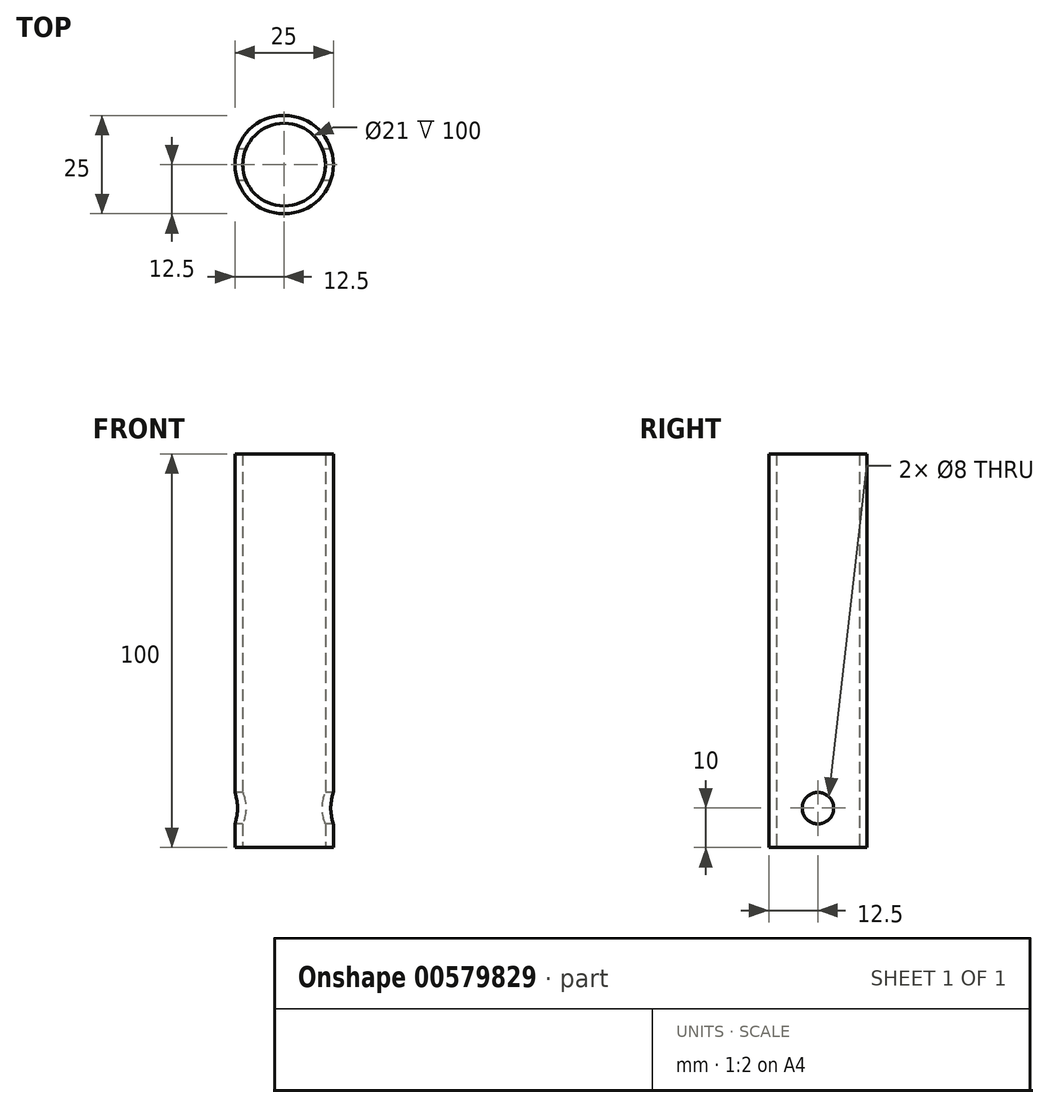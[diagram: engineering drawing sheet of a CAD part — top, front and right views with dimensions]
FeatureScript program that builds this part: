
annotation { "Feature Type Name" : "Feature", "Feature Type Description" : "" }
export const myFeature = defineFeature(function(context is Context, id is Id, definition is map)
    precondition{}
    {
        {
            var Q0;
            Q0=qCreatedBy(makeId("Top.planeOp"),FACE);
            var sketch = newSketch(context, id + "F0", { "sketchPlane" : qUnion([Q0])});
            skCircle(sketch, "E0", {"center": v(0, 0) * mm, "radius": 12.5 * mm});
            skSolve(sketch);
        }
        {
            var Q0;
            Q0=makeQuery(id+"F0.imprint","IMPRINT",FACE,{"disambiguationData":[TD([[makeQuery(id+"F0.imprint","IMPRINT",EDGE,{"derivedFrom":sQuery(id+"F0.wireOp",EDGE,"E0")}),1.0]])]});
            extrude(context, id + "F1", {"entities" : qUnion([Q0]), "depth" : 100 * mm, "offsetDistance" : 25 * mm});
        }
        {
            var Q0;
            Q0=makeQuery(id+"F1.opExtrude","CAP_FACE",FACE,{"disambiguationData":[OSD([sQuery(id+"F0.wireOp",EDGE,"E0")])],"isStart":false});
            var Q1;
            Q1=makeQuery(id+"F1.opExtrude","CAP_FACE",FACE,{"disambiguationData":[OSD([sQuery(id+"F0.wireOp",EDGE,"E0")])],"isStart":true});
            shell(context, id + "F2", {"entities" : qUnion([Q0, Q1]), "thickness" : 2 * mm});
        }
        {
            var Q0;
            Q0=qCreatedBy(makeId("Right.planeOp"),FACE);
            cPlane(context, id + "F3", {"entities" : qUnion([Q0]), "cplaneType" : CPlaneType.OFFSET, "offset" : 30 * mm, "oppositeDirection" : true, "width" : 150 * mm, "height" : 150 * mm});
        }
        {
            var Q0;
            Q0=qCreatedBy(id+"F3.planeOp",FACE);
            var sketch = newSketch(context, id + "F4", { "sketchPlane" : qUnion([Q0])});
            skPoint(sketch, "E1", {"position": v(0, 10) * mm});
            skSolve(sketch);
        }
        {
            var Q0;
            Q0=sQuery(id+"F4.wireOp",VERTEX,"E1");
            var Q1;
            Q1=makeQuery(id+"F1.opExtrude","SWEPT_BODY",BODY,{"disambiguationData":[OSD([sQuery(id+"F0.wireOp",EDGE,"E0")])]});
            hole(context, id + "F5", {"style" : HoleStyle.SIMPLE, "endStyle" : HoleEndStyle.THROUGH, "oppositeDirection" : true, "holeDiameter" : 8 * mm, "isTappedThrough" : true, "tappedDepth" : 12 * mm, "tapClearance" : 3, "locations" : qUnion([Q0]), "scope" : qUnion([Q1])});
        }
    });
